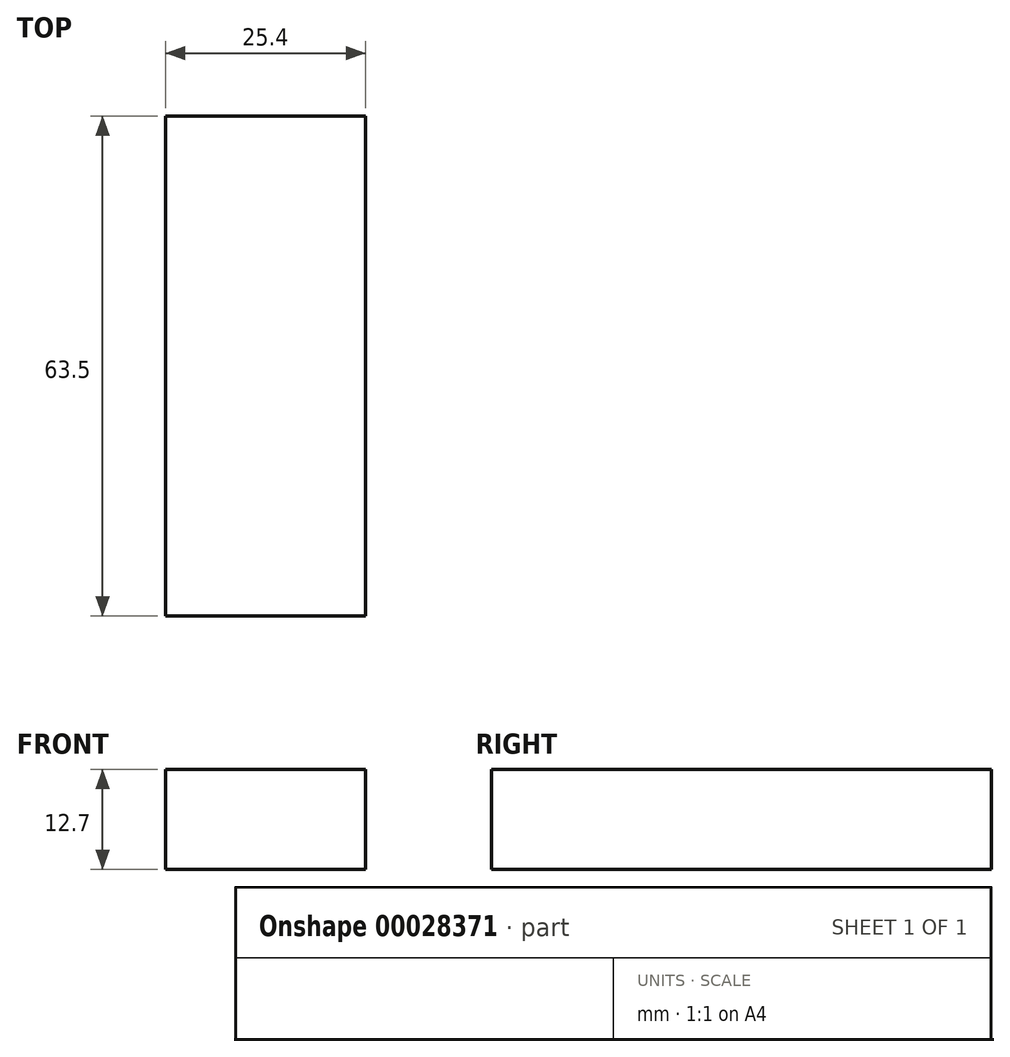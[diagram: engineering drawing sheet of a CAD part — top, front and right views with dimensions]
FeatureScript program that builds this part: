
annotation { "Feature Type Name" : "Feature", "Feature Type Description" : "" }
export const myFeature = defineFeature(function(context is Context, id is Id, definition is map)
    precondition{}
    {
        {
            var Q0;
            Q0=qCreatedBy(makeId("Top.planeOp"),FACE);
            var sketch = newSketch(context, id + "F0", { "sketchPlane" : qUnion([Q0])});
            skLineSegment(sketch, "E0.rect.bottom", {"start": v(-12.7, 31.75) * mm, "end": v(12.7, 31.75) * mm});
            skLineSegment(sketch, "E0.rect.top", {"start": v(-12.7, -31.75) * mm, "end": v(12.7, -31.75) * mm});
            skLineSegment(sketch, "E0.rect.left", {"start": v(-12.7, 31.75) * mm, "end": v(-12.7, -31.75) * mm});
            skLineSegment(sketch, "E0.rect.right", {"start": v(12.7, 31.75) * mm, "end": v(12.7, -31.75) * mm});
            skPoint(sketch, "E0.rect.middle", {"position": v(0, 0) * mm});
            skSolve(sketch);
        }
        {
            var Q0;
            Q0=makeQuery(id+"F0.imprint","IMPRINT",FACE,{"disambiguationData":[TD([[makeQuery(id+"F0.imprint","IMPRINT",EDGE,{"derivedFrom":sQuery(id+"F0.wireOp",EDGE,"E0.rect.bottom")}),-1.0]])]});
            extrude(context, id + "F1", {"entities" : qUnion([Q0]), "depth" : 12.7 * mm});
        }
    });
